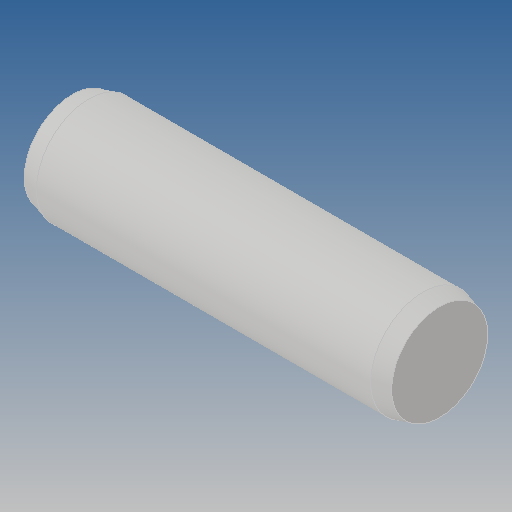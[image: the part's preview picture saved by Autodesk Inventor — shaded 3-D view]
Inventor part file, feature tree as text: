
AUTODESK INVENTOR PART (.ipt)
format: ipt  version: 2018 (Build 220112000, 112)  size: 103,936 bytes
history: native  units: mm
features: extrude x1
ambient origin geometry x8: Origin, YZ Plane, XZ Plane, XY Plane, X Axis, Y Axis, Z Axis, Center Point
bodies: Solid1 (feature_tree)
feature tree (1):
  extrude  "Extrude3"  [1 undecoded]
note: 1 required parameter value undecoded (feature->parameter linkage not recoverable at this tier; creation-order binding heuristic only, values carry confidence <= 0.55)
